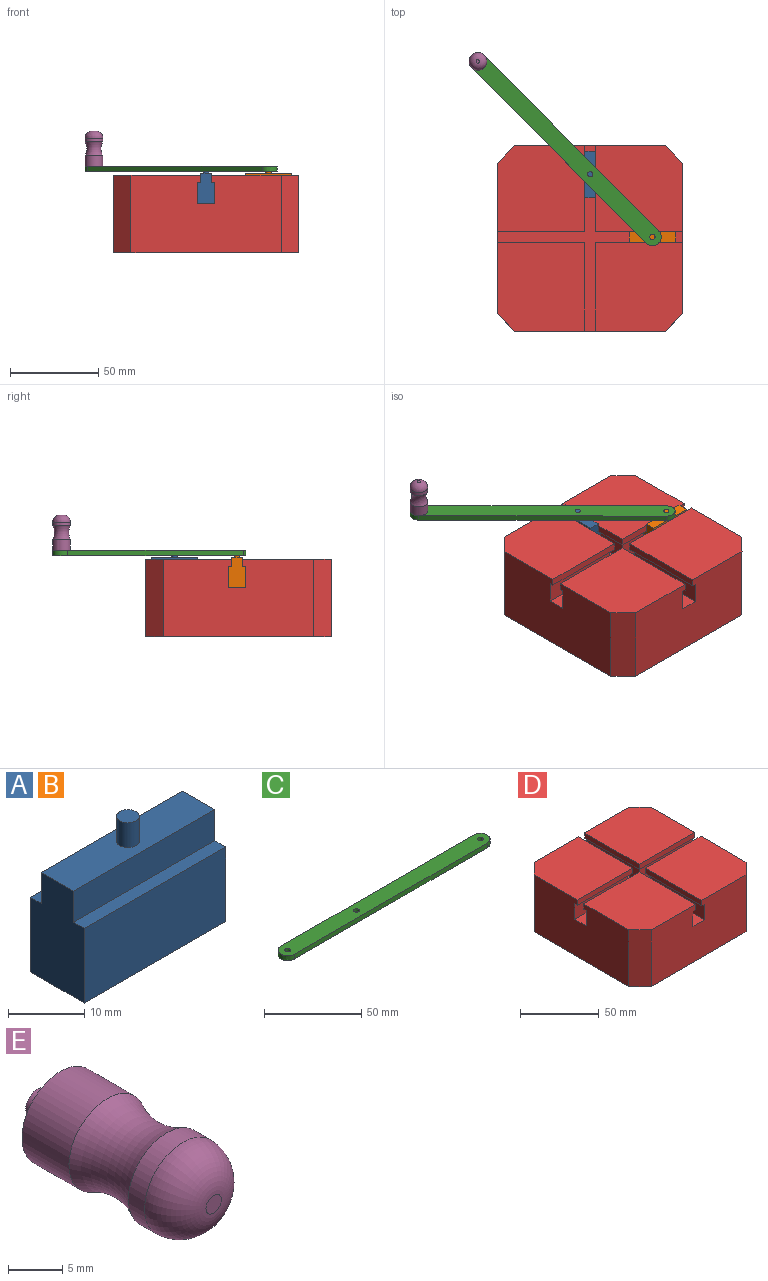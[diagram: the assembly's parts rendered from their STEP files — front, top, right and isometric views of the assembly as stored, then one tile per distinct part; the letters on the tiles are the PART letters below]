
ASSEMBLY  parts=5 mates=5
PART A: 12 faces, bbox 26.2x10x21 mm
  f0: plane 26.25x2mm, normal (0,0,1), area 52.5mm2, adj f1,f2,f3,f7
  f1: plane 17x10mm, normal (-1,0,0), area 150mm2, adj f0,f2,f4,f5,f6,f7,f8,f9
  f2: plane 26.25x12mm, normal (0,-1,0), area 315mm2, adj f0,f1,f3,f5
  f3: plane 17x10mm, normal (1,0,0), area 150mm2, adj f0,f2,f4,f5,f6,f7,f8,f9
  f4: plane 26.25x12mm, normal (0,1,0), area 315mm2, adj f1,f3,f5,f6
  f5: plane 26.25x10mm, normal (0,0,-1), area 262.5mm2, adj f1,f2,f3,f4
  f6: plane 26.25x2mm, normal (0,0,1), area 52.5mm2, adj f1,f3,f4,f8
  f7: plane 26.25x5mm, normal (0,-1,0), area 131.2mm2, adj f0,f1,f3,f9
  f8: plane 26.25x5mm, normal (0,1,0), area 131.2mm2, adj f1,f3,f6,f9
  f9: plane 26.25x6mm, normal (0,0,1), area 150.4mm2, adj f1,f3,f7,f8,f10
  f10: cylinder r=1.5mm len=4mm, axis (0,0,-1), area 37.7mm2, adj f9,f11
  f11: plane 3x3mm, normal (0,0,1), area 7.1mm2, adj f10
PART B: same geometry as A
PART C: 9 faces, bbox 151.5x10x3 mm
  f0: plane 140x3mm, normal (0,1,0), area 420mm2, adj f1,f6,f7,f8
  f1: extruded ~10x5mm, area 47.1mm2, adj f0,f2,f7,f8
  f2: plane 140x3mm, normal (0,-1,0), area 420mm2, adj f1,f6,f7,f8
  f3: cylinder r=1.5mm len=3mm, axis (0,0,-1), area 28.3mm2, adj f7,f8
  f4: cylinder r=1.5mm len=3mm, axis (0,0,-1), area 28.3mm2, adj f7,f8
  f5: cylinder r=1.5mm len=3mm, axis (0,0,-1), area 28.3mm2, adj f7,f8
  f6: cylinder r=5mm len=10mm, axis (0,0,-1), area 47.1mm2, adj f0,f2,f7,f8
  f7: plane 151.5x10mm, normal (0,0,1), area 1457.3mm2, adj f0,f1,f2,f3,f4,f5,f6
  f8: plane 151.5x10mm, normal (0,0,-1), area 1457.3mm2, adj f0,f1,f2,f3,f4,f5,f6
PART D: 34 faces, bbox 105x105x44 mm
  f0: plane 85x44mm, normal (1,0,0), area 3596mm2, adj f8,f9,f10,f13,f14,f21,f22,f25
  f1: plane 85x44mm, normal (-1,0,0), area 3596mm2, adj f6,f7,f11,f12,f13,f17,f18,f23
  f2: plane 48.32x12mm, normal (1,0,0), area 579.8mm2, adj f5,f24,f28,f32
  f3: plane 48.32x12mm, normal (-1,0,0), area 579.8mm2, adj f5,f26,f28,f30
  f4: plane 85x44mm, normal (0,1,0), area 3596mm2, adj f6,f8,f10,f11,f13,f15,f16,f23
  f5: plane 85x44mm, normal (0,-1,0), area 3596mm2, adj f2,f3,f7,f9,f12,f13,f14,f19
  f6: plane 49.5x48.68mm, normal (0,0,1), area 2359.7mm2, adj f1,f4,f11,f16,f17
  f7: plane 50.32x49.5mm, normal (0,0,1), area 2440.8mm2, adj f1,f5,f12,f18,f19
  f8: plane 49.5x48.68mm, normal (0,0,1), area 2359.7mm2, adj f0,f4,f10,f15,f22
  f9: plane 44x10mm, normal (0.71,-0.71,0), area 622.3mm2, adj f0,f5,f13,f14
  f10: plane 44x10mm, normal (0.71,0.71,0), area 622.3mm2, adj f0,f4,f8,f13
  f11: plane 44x10mm, normal (-0.71,0.71,0), area 622.3mm2, adj f1,f4,f6,f13
  f12: plane 44x10mm, normal (-0.71,-0.71,0), area 622.3mm2, adj f1,f5,f7,f13
  f13: plane 105x105mm, normal (0,0,-1), area 10825mm2, adj f0,f1,f4,f5,f9,f10,f11,f12
  f14: plane 50.32x49.5mm, normal (0,0,1), area 2440.8mm2, adj f0,f5,f9,f20,f21
  f15: plane 48.68x4mm, normal (-1,0,0), area 194.7mm2, adj f4,f8,f22,f25
  f16: plane 48.68x4mm, normal (1,0,0), area 194.7mm2, adj f4,f6,f17,f23
  f17: plane 49.5x4mm, normal (0,-1,0), area 198mm2, adj f1,f6,f16,f23
  f18: plane 49.5x4mm, normal (0,1,0), area 198mm2, adj f1,f7,f19,f24
  f19: plane 50.32x4mm, normal (1,0,0), area 201.3mm2, adj f5,f7,f18,f24
  f20: plane 50.32x4mm, normal (-1,0,0), area 201.3mm2, adj f5,f14,f21,f26
  f21: plane 49.5x4mm, normal (0,1,0), area 198mm2, adj f0,f14,f20,f26
  f22: plane 49.5x4mm, normal (0,-1,0), area 198mm2, adj f0,f8,f15,f25
  f23: plane 49.5x48.68mm, normal (0,0,-1), area 192.4mm2, adj f1,f4,f16,f17,f27,f33
  f24: plane 50.32x49.5mm, normal (0,0,-1), area 195.6mm2, adj f1,f2,f5,f18,f19,f32
  f25: plane 49.5x48.68mm, normal (0,0,-1), area 192.4mm2, adj f0,f4,f15,f22,f29,f31
  f26: plane 50.32x49.5mm, normal (0,0,-1), area 195.6mm2, adj f0,f3,f5,f20,f21,f30
  f27: plane 46.68x12mm, normal (1,0,0), area 560.2mm2, adj f4,f23,f28,f33
  f28: plane 105x105mm, normal (0,0,1), area 2000mm2, adj f0,f1,f2,f3,f4,f5,f27,f29
  f29: plane 46.68x12mm, normal (-1,0,0), area 560.2mm2, adj f4,f25,f28,f31
  f30: plane 47.5x12mm, normal (0,1,0), area 570mm2, adj f0,f3,f26,f28
  f31: plane 47.5x12mm, normal (0,-1,0), area 570mm2, adj f0,f25,f28,f29
  f32: plane 47.5x12mm, normal (0,1,0), area 570mm2, adj f1,f2,f24,f28
  f33: plane 47.5x12mm, normal (0,-1,0), area 570mm2, adj f1,f23,f27,f28
PART E: 8 faces, bbox 13.7x23x13.7 mm
  f0: plane 2x2mm, normal (0,-1,0), area 3.1mm2, adj f1
  f1: torus R=1mm, axis (0,-1,0), area 140mm2, adj f0,f2
  f2: cylinder r=5mm len=10mm, axis (0,-1,0), area 66.8mm2, adj f1,f3
  f3: torus R=12mm, axis (0,-1,0), area 220.3mm2, adj f2,f4
  f4: cylinder r=5mm len=10mm, axis (0,-1,0), area 192.5mm2, adj f3,f5
  f5: plane 10x10mm, normal (0,1,0), area 71.5mm2, adj f4,f6
  f6: cylinder r=1.5mm len=3mm, axis (0,-1,0), area 28.3mm2, adj f5,f7
  f7: plane 3x3mm, normal (0,1,0), area 7.1mm2, adj f6
PLACE A rot(axis=(0,0,-1),90deg) t=(-118.54,-29.25,-42.75)mm
PLACE B rot(axis=(0.99,0.11,0.04),0deg) t=(-83.28,-64.7,-42.75)mm
PLACE C rot(axis=(0,0,1),134.9deg) t=(-132.65,-15.07,-36.75)mm
PLACE D rot(axis=(0.99,0.11,0.04),0deg) t=(-118.54,-64.7,-38.75)mm fixed
PLACE E rot(axis=(-0.86,-0.36,0.36),98.4deg) t=(-180.2,36.35,-24.82)mm
MATE revolute C.f3 <-> B.f10  axis (0,0,1) through (-83.28,-64.7,-33.75)mm
MATE revolute C.f4 <-> A.f10  axis (0,0,1) through (-118.54,-29.25,-33.75)mm
MATE slider D.f1 <-> B.f1  axis (-1,0,0) through (-171.04,-64.7,-54.75)mm
MATE fastened E.f1 <-> C.f5  axis (0,0,-1) through (-182.02,34.55,-36.75)mm
MATE slider A.f3 <-> D.f5  axis (0,-1,0) through (-118.54,-42.38,-54.75)mm
